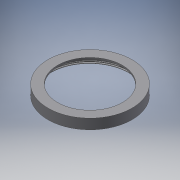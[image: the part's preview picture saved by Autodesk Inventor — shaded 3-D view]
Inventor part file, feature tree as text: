
AUTODESK INVENTOR PART (.ipt)
format: ipt  version: 2016 SP2 (Build 200236200, 236)  size: 300,032 bytes
history: native  units: mm
features: sketch x3, revolve x2, thread x1, other x1
ambient origin geometry x8: Origin, YZ Plane, XZ Plane, XY Plane, X Axis, Y Axis, Z Axis, Center Point
bodies: Volumenkörper1 (feature_tree), Volumenkörper4 (feature_tree)
feature tree (7):
  revolve  "Umdrehung1"
  thread  "Gewinde3"  [1 undecoded]
  revolve  "Umdrehung4"
  other  "Spirale3"
  sketch  "Skizze2"  dims[d1=3.0mm]
  sketch  "Skizze7"  dims[d3=7.0mm]
  sketch  "Skizze8"  dims[d4=8.5mm d5=2.0mm d6=50.0mm d7=0.0mm d8=90.0deg d18=60.0deg d29=3.0mm d39=60.0deg d50=10.0mm d51=0.0mm d52=60.0deg d53=0.320166mm d54=0.320166mm d57=2.0mm d59=60.0deg d61=0.0mm d62=2.002mm d63=7.0mm d64=10.0mm d65=0.0mm d66=0.0mm d67=0.0mm d68=0.0mm d69=0.0mm]
note: 1 required parameter value undecoded (feature->parameter linkage not recoverable at this tier; creation-order binding heuristic only, values carry confidence <= 0.55)
